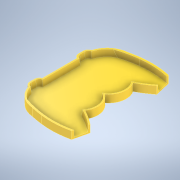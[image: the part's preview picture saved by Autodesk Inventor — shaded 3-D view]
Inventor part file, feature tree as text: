
AUTODESK INVENTOR PART (.ipt)
format: ipt  version: 2022 (Build 260153000, 153)  size: 418,304 bytes
history: native  units: mm
features: chamfer x9, sketch x3, extrude x2
ambient origin geometry x8: Origin, YZ Plane, XZ Plane, XY Plane, X Axis, Y Axis, Z Axis, Center Point
bodies: Solid1 (feature_tree)
feature tree (14):
  sketch  "Sketch1"  dims[d0=35.0mm d1=60.0mm]
  extrude  "Extrusion1"  Depth=60.0mm
  extrude  "Extrusion2"  Depth=25.0mm
  chamfer  "Chamfer1"  Distance=25.0mm
  chamfer  "Chamfer2"  Distance=27.0mm
  chamfer  "Chamfer3"  Distance=34.0mm
  chamfer  "Chamfer4"  Distance=27.0mm
  chamfer  "Chamfer5"  Distance=7.5mm
  chamfer  "Chamfer6"  Distance=25.0mm
  chamfer  "Chamfer7"  Distance=27.0mm
  chamfer  "Chamfer8"  Distance=6.0mm
  chamfer  "Chamfer9"  Distance=6.0mm
  sketch  "Sketch2"  dims[d2=17.5mm d3=25.0mm]
  sketch  "Sketch4"  dims[d4=22.5mm d6=25.0mm d7=27.0mm d8=34.0mm d9=27.0mm d10=7.5mm d11=25.0mm d12=27.0mm d13=34.0mm d14=27.0mm d15=6.0mm d16=6.0mm d17=6.0mm d18=6.5mm d22=6.0mm d23=40.0mm d25=360.0deg d27=25.0mm d28=27.0mm d31=40.0mm d32=25.0mm d33=27.0mm d34=5.0mm d35=8.0mm d36=8.0mm d37=35.0mm d38=8.0mm d39=12.0mm d40=8.0mm d41=60.0mm d42=17.5mm d47=4.0mm d48=7.5mm d49=22.5mm d50=25.0mm d51=27.0mm d52=34.0mm d53=6.5mm d54=3.0mm d55=3.0mm d56=6.0mm d57=6.0mm d58=40.0mm d60=360.0deg d62=50.0mm d63=12.0mm d64=0.0mm d65=1.5mm d66=12.5mm d67=27.0mm d68=25.0mm d69=1.401mm d70=13.425896mm d71=200.0mm d72=37.3mm d73=4.0mm d74=37.3mm d75=15.0mm d76=15.0mm d77=30.0mm d78=30.0mm d79=48.0mm d80=9.0mm d81=9.0mm d82=3.0mm d83=3.0mm d84=3.0mm d85=3.0mm d86=6.5mm d87=14.0mm d88=3.0mm d89=1.5mm d90=1.5mm d91=3.0mm d92=3.0mm d93=3.0mm d94=3.0mm d95=3.0mm d96=3.0mm d97=2.0mm d98=0.0mm d99=1.0mm d100=10.0mm d101=45.0deg d102=1.0mm d103=10.0mm d104=45.0deg d105=1.0mm d106=10.0mm d107=45.0deg d108=1.0mm d109=10.0mm d110=45.0deg d111=1.0mm d112=10.0mm d113=45.0deg d114=1.0mm d115=10.0mm d116=45.0deg d117=1.0mm d118=10.0mm d119=45.0deg d120=1.0mm d121=10.0mm d122=45.0deg d123=1.0mm d124=10.0mm d125=45.0deg]
